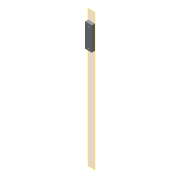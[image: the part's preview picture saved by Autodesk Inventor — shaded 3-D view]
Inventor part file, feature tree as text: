
AUTODESK INVENTOR PART (.ipt)
format: ipt  version: 2019.4 (Build 234330000, 330)  size: 105,472 bytes
history: native  units: mm
features: other x3, extrude x2, sketch x2, plane x1, reference x1, projected_geometry x1
ambient origin geometry x8: Origin, YZ Plane, XZ Plane, XY Plane, X Axis, Y Axis, Z Axis, Center Point
bodies: Solid1 (feature_tree)
feature tree (10):
  plane  "Work Plane1"
  extrude  "Extrusion1"  Depth=4.0mm
  extrude  "Extrusion2"  Depth=3.0mm
  sketch  "Sketch1"  dims[d0=4.0mm d1=4.0mm]
  reference  "Reference1"
  sketch  "Sketch2"  dims[d2=2.9mm d3=2.9mm d4=5.0mm d5=0.0mm d6=4.9mm d7=4.9mm d8=0.5mm d10=0.5mm d11=3.0mm d12=0.0mm]
  projected_geometry  "Projected Loop1"
  other  "Assembly_Opentrons_Imagingunit_v1.iam"
  other  "Assembly_opentrons_microscope_slide_y:1"
  other  "00_MGN12 LINEAR GUIDE RAIL, CONFIGURABLE:1"
